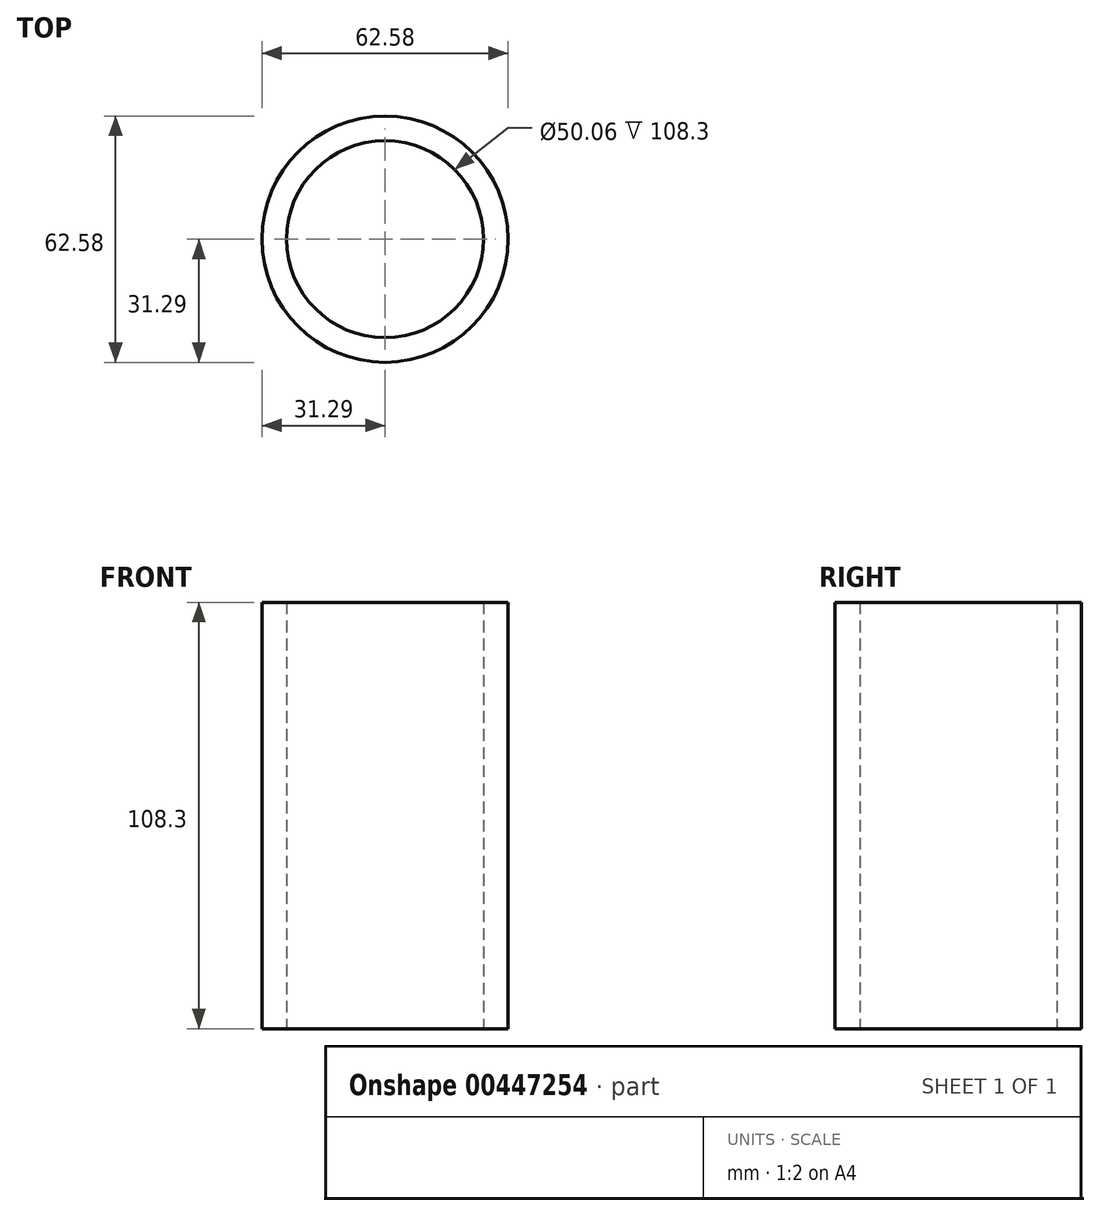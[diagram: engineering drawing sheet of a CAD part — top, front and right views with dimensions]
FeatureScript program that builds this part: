
annotation { "Feature Type Name" : "Feature", "Feature Type Description" : "" }
export const myFeature = defineFeature(function(context is Context, id is Id, definition is map)
    precondition{}
    {
        {
            var Q0;
            Q0=qCreatedBy(makeId("Top.planeOp"),FACE);
            var sketch = newSketch(context, id + "F0", { "sketchPlane" : qUnion([Q0])});
            skCircle(sketch, "E0", {"center": v(0, 0) * mm, "radius": 31.3 * mm});
            skCircle(sketch, "E1", {"center": v(0, 0) * mm, "radius": 25.03 * mm});
            skSolve(sketch);
        }
        {
            var Q0;
            Q0=makeQuery(id+"F0.imprint","IMPRINT",FACE,{"disambiguationData":[TD([[makeQuery(id+"F0.imprint","IMPRINT",EDGE,{"derivedFrom":sQuery(id+"F0.wireOp",EDGE,"E0")}),1.0]])]});
            extrude(context, id + "F1", {"entities" : qUnion([Q0]), "depth" : 108.3 * mm});
        }
    });
